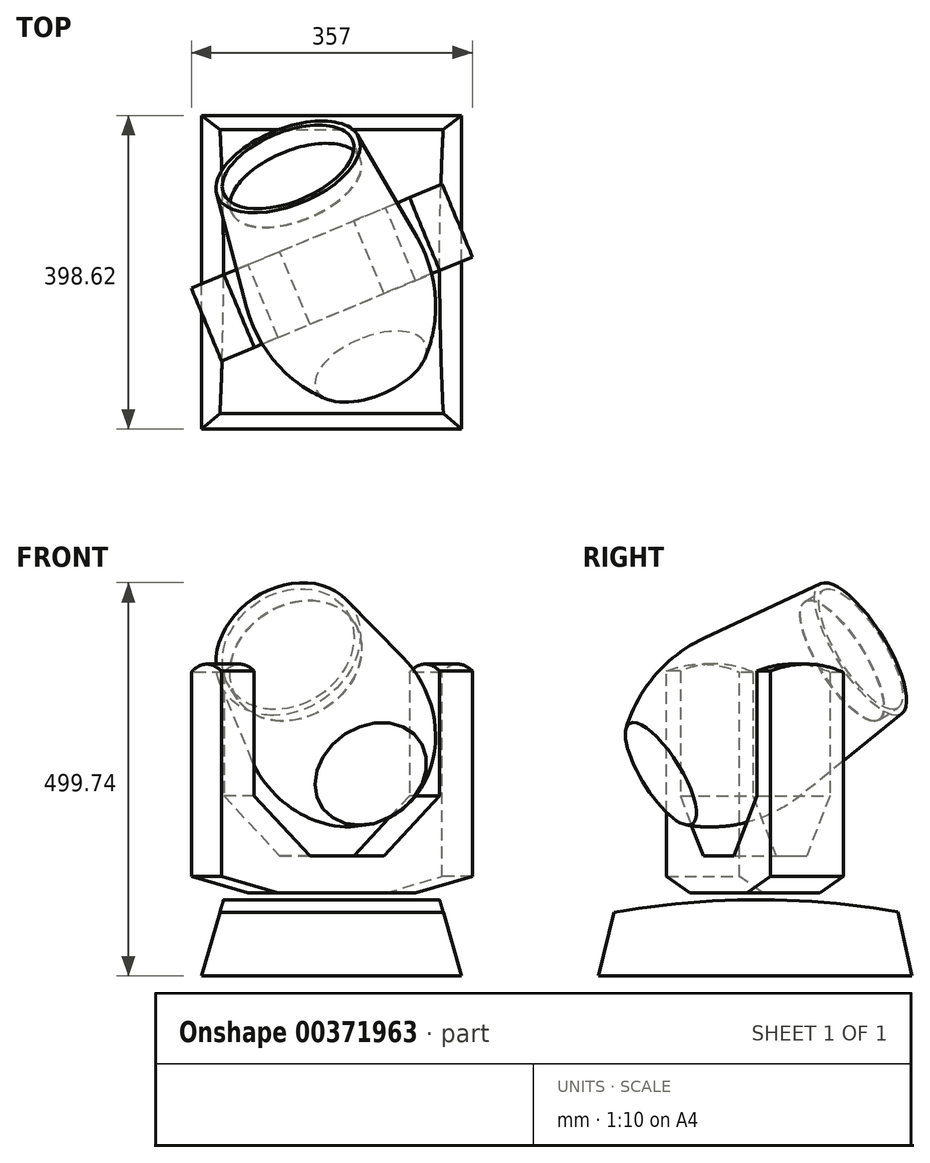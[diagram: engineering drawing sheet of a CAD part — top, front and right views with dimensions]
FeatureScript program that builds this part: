
annotation { "Feature Type Name" : "Feature", "Feature Type Description" : "" }
export const myFeature = defineFeature(function(context is Context, id is Id, definition is map)
    precondition{}
    {
        {
            var Q0;
            Q0=qCreatedBy(makeId("Front.planeOp"),FACE);
            var sketch = newSketch(context, id + "F0", { "sketchPlane" : qUnion([Q0])});
            skLineSegment(sketch, "E0.bottom", {"start": v(164.65, -50) * mm, "end": v(-165.35, -50) * mm});
            skLineSegment(sketch, "E0.top", {"start": v(136.02, 50) * mm, "end": v(-136.72, 50) * mm});
            skPoint(sketch, "E0.middle", {"position": v(0, 0) * mm});
            skLineSegment(sketch, "E1", {"start": v(-165.35, -50) * mm, "end": v(-136.72, 50) * mm});
            skLineSegment(sketch, "E2", {"start": v(164.65, -50) * mm, "end": v(136.02, 50) * mm});
            skPoint(sketch, "E0.right.end.orphan", {"position": v(-164.65, 50) * mm});
            skPoint(sketch, "E3.orphan", {"position": v(165.35, 50) * mm});
            skLineSegment(sketch, "E4", {"start": v(-0.35, -50) * mm, "end": v(-0.35, 50) * mm, "construction": true});
            skSolve(sketch);
        }
        {
            var Q0;
            Q0 = qSketchRegion(id + "F0", true);
            extrude(context, id + "F1", {"entities" : qUnion([Q0]), "depth" : 200 * mm, "hasSecondDirection" : true, "secondDirectionOppositeDirection" : true, "secondDirectionDepth" : 200 * mm});
        }
        {
            var Q0;
            Q0=qCreatedBy(makeId("Right.planeOp"),FACE);
            var sketch = newSketch(context, id + "F2", { "sketchPlane" : qUnion([Q0])});
            skLineSegment(sketch, "E5", {"start": v(199.65, -50.3) * mm, "end": v(181.5, 31.39) * mm});
            skLineSegment(sketch, "E6", {"start": v(199.65, -50.3) * mm, "end": v(-199.12, -50.3) * mm});
            skLineSegment(sketch, "E7", {"start": v(-199.12, -50.3) * mm, "end": v(-179.02, 30.74) * mm});
            skArc(sketch, "E8", {"start": v(181.5, 31.39) * mm, "mid": v(1.21, 47.02) * mm, "end": v(-179.02, 30.74) * mm});
            skLineSegment(sketch, "E9.bottom", {"start": v(207.43, 59.92) * mm, "end": v(-206.9, 59.92) * mm});
            skLineSegment(sketch, "E9.top", {"start": v(207.43, -57.44) * mm, "end": v(-206.9, -57.44) * mm});
            skLineSegment(sketch, "E9.left", {"start": v(207.43, 59.92) * mm, "end": v(207.43, -57.44) * mm});
            skLineSegment(sketch, "E9.right", {"start": v(-206.9, 59.92) * mm, "end": v(-206.9, -57.44) * mm});
            skSolve(sketch);
        }
        {
            var Q0;
            Q0 = qSketchRegion(id + "F2", true);
            extrude(context, id + "F3", {"entities" : qUnion([Q0]), "operationType" : NewBodyOperationType.REMOVE, "endBound" : BoundingType.THROUGH_ALL, "oppositeDirection" : true, "depth" : 25 * mm, "hasSecondDirection" : true, "secondDirectionBound" : SecondDirectionBoundingType.THROUGH_ALL, "secondDirectionOppositeDirection" : false, "secondDirectionDepth" : 25 * mm});
        }
        {
            var Q0;
            Q0=qCreatedBy(makeId("Front.planeOp"),FACE);
            var sketch = newSketch(context, id + "F4", { "sketchPlane" : qUnion([Q0])});
            skLineSegment(sketch, "E10", {"start": v(0, 0) * mm, "end": v(0, 55.5) * mm, "construction": true});
            skLineSegment(sketch, "E11", {"start": v(94.5, 55.5) * mm, "end": v(0, 55.5) * mm});
            skLineSegment(sketch, "E12", {"start": v(94.5, 55.5) * mm, "end": v(172.5, 76.57) * mm});
            skLineSegment(sketch, "E13", {"start": v(172.5, 76.57) * mm, "end": v(172.5, 350) * mm});
            skLineSegment(sketch, "E14", {"start": v(172.5, 350) * mm, "end": v(127.55, 350) * mm});
            skLineSegment(sketch, "E15", {"start": v(127.55, 350) * mm, "end": v(127.55, 179.09) * mm});
            skLineSegment(sketch, "E16", {"start": v(127.55, 179.09) * mm, "end": v(50.95, 102.49) * mm});
            skLineSegment(sketch, "E17", {"start": v(50.95, 102.49) * mm, "end": v(0, 102.49) * mm});
            skLineSegment(sketch, "E18.MirrorCS", {"start": v(-127.55, 179.09) * mm, "end": v(-50.95, 102.49) * mm});
            skLineSegment(sketch, "E19.MirrorCS", {"start": v(-50.95, 102.49) * mm, "end": v(0, 102.49) * mm});
            skLineSegment(sketch, "E20.MirrorCS", {"start": v(-127.55, 350) * mm, "end": v(-127.55, 179.09) * mm});
            skLineSegment(sketch, "E21.MirrorCS", {"start": v(-172.5, 350) * mm, "end": v(-127.55, 350) * mm});
            skLineSegment(sketch, "E22.MirrorCS", {"start": v(-94.5, 55.5) * mm, "end": v(0, 55.5) * mm});
            skLineSegment(sketch, "E23.MirrorCS", {"start": v(-172.5, 76.57) * mm, "end": v(-172.5, 350) * mm});
            skLineSegment(sketch, "E24.MirrorCS", {"start": v(-94.5, 55.5) * mm, "end": v(-172.5, 76.57) * mm});
            skSolve(sketch);
        }
        {
            var Q0;
            Q0 = qSketchRegion(id + "F4", true);
            extrude(context, id + "F5", {"entities" : qUnion([Q0]), "depth" : 50 * mm, "hasSecondDirection" : true, "secondDirectionOppositeDirection" : true, "secondDirectionDepth" : 50 * mm});
        }
        {
            var Q0;
            Q0=qCreatedBy(makeId("Right.planeOp"),FACE);
            var sketch = newSketch(context, id + "F6", { "sketchPlane" : qUnion([Q0])});
            skArc(sketch, "E25", {"start": v(57.41, 332.46) * mm, "mid": v(-0.95, 346.34) * mm, "end": v(-59.48, 333.23) * mm});
            skLineSegment(sketch, "E26", {"start": v(57.41, 332.46) * mm, "end": v(57.41, 368.6) * mm});
            skLineSegment(sketch, "E27", {"start": v(57.41, 368.6) * mm, "end": v(-58.72, 368.6) * mm});
            skLineSegment(sketch, "E28", {"start": v(-58.72, 368.6) * mm, "end": v(-59.48, 333.23) * mm});
            skSolve(sketch);
        }
        {
            var Q0;
            Q0 = qSketchRegion(id + "F6", true);
            extrude(context, id + "F7", {"entities" : qUnion([Q0]), "operationType" : NewBodyOperationType.REMOVE, "endBound" : BoundingType.THROUGH_ALL, "oppositeDirection" : true, "depth" : 25 * mm, "hasSecondDirection" : true, "secondDirectionBound" : SecondDirectionBoundingType.THROUGH_ALL, "secondDirectionOppositeDirection" : false, "secondDirectionDepth" : 25 * mm});
        }
        {
            var Q0;
            Q0=qCreatedBy(makeId("Right.planeOp"),FACE);
            var sketch = newSketch(context, id + "F8", { "sketchPlane" : qUnion([Q0])});
            skLineSegment(sketch, "E29", {"start": v(172.17, 264.85) * mm, "end": v(-144.94, 264.85) * mm});
            skLineSegment(sketch, "E30", {"start": v(172.17, 264.85) * mm, "end": v(172.17, 362.16) * mm});
            skLineSegment(sketch, "E31", {"start": v(172.17, 362.16) * mm, "end": v(0, 382.08) * mm});
            skArc(sketch, "E32", {"start": v(0, 382.08) * mm, "mid": v(-76.7, 375.65) * mm, "end": v(-144.94, 340.02) * mm});
            skLineSegment(sketch, "E33", {"start": v(-144.94, 264.85) * mm, "end": v(-144.94, 340.02) * mm});
            skSolve(sketch);
        }
        {
            var Q0;
            Q0 = qSketchRegion(id + "F8", true);
            var Q1;
            Q1=sQuery(id+"F8.wireOp",EDGE,"E29");
            revolve(context, id + "F9", {"entities" : qUnion([Q0]), "axis" : qUnion([Q1]), "revolveType" : RevolveType.FULL});
        }
        {
            var Q0;
            Q0=makeQuery(id+"F9.opRevolve","SWEPT_FACE",FACE,{"disambiguationData":[OSD([sQuery(id+"F8.wireOp",EDGE,"E30")])]});
            var sketch = newSketch(context, id + "F10", { "sketchPlane" : qUnion([Q0])});
            skCircle(sketch, "E34", {"center": v(0, 264.85) * mm, "radius": 88.64 * mm});
            skSolve(sketch);
        }
        {
            var Q0;
            Q0 = qSketchRegion(id + "F10", true);
            extrude(context, id + "F11", {"entities" : qUnion([Q0]), "operationType" : NewBodyOperationType.REMOVE, "oppositeDirection" : true, "depth" : 30 * mm});
        }
        {
            var Q0;
            Q0=makeQuery(id+"F11.boolean.opBoolean","COPY",FACE,{"derivedFrom":makeQuery(id+"F11.opExtrude","CAP_FACE",FACE,{"disambiguationData":[OSD([sQuery(id+"F10.wireOp",EDGE,"E34")])],"isStart":false})});
            var sketch = newSketch(context, id + "F12", { "sketchPlane" : qUnion([Q0])});
            skCircle(sketch, "E35.0", {"center": v(0, 264.85) * mm, "radius": 88.64 * mm});
            skSolve(sketch);
        }
        {
            var Q0;
            Q0 = qSketchRegion(id + "F12", true);
            extrude(context, id + "F13", {"entities" : qUnion([Q0]), "depth" : 1 * mm});
        }
        {
            var Q0;
            Q0=qCreatedBy(makeId("Top.planeOp"),FACE);
            cPlane(context, id + "F14", {"entities" : qUnion([Q0]), "cplaneType" : CPlaneType.OFFSET, "offset" : 265 * mm, "width" : 150 * mm, "height" : 150 * mm});
        }
        {
            var Q0;
            Q0=makeQuery(id+"F3.boolean.opBoolean","COPY",EDGE,{"derivedFrom":makeQuery(id+"F3.opExtrude","SWEPT_EDGE",EDGE,{"disambiguationData":[OSD([sQuery(id+"F2.wireOp",EDGE,"E5"),sQuery(id+"F2.wireOp",EDGE,"E8")])]})});
            var Q1;
            Q1=qCreatedBy(id+"F14.planeOp",FACE);
            cPlane(context, id + "F15", {"entities" : qUnion([Q0, Q1]), "cplaneType" : CPlaneType.LINE_ANGLE, "offset" : 25 * mm, "angle" : 15 * degree, "width" : 150 * mm, "height" : 150 * mm});
        }
        {
            var Q0;
            Q0=qCreatedBy(id+"F15.planeOp",FACE);
            cPlane(context, id + "F16", {"entities" : qUnion([Q0]), "cplaneType" : CPlaneType.OFFSET, "offset" : 280 * mm, "oppositeDirection" : true, "width" : 150 * mm, "height" : 150 * mm});
        }
        {
            var Q0;
            Q0=makeQuery(id+"F9.opRevolve","SWEPT_BODY",BODY,{"disambiguationData":[OSD([sQuery(id+"F8.wireOp",EDGE,"E29"),sQuery(id+"F8.wireOp",EDGE,"E30"),sQuery(id+"F8.wireOp",EDGE,"E31"),sQuery(id+"F8.wireOp",EDGE,"E32"),sQuery(id+"F8.wireOp",EDGE,"E33")])]});
            var Q1;
            Q1=makeQuery(id+"F13.opExtrude","SWEPT_BODY",BODY,{"disambiguationData":[OSD([sQuery(id+"F12.wireOp",EDGE,"E35.0")])]});
            var Q2;
            Q2=qCreatedBy(id+"F16.planeOp",FACE);
            mirror(context, id + "F17", {"entities" : qUnion([Q0, Q1]), "mirrorPlane" : qUnion([Q2])});
        }
        {
            var Q0;
            Q0=makeQuery(id+"F9.opRevolve","SWEPT_BODY",BODY,{"disambiguationData":[OSD([sQuery(id+"F8.wireOp",EDGE,"E29"),sQuery(id+"F8.wireOp",EDGE,"E30"),sQuery(id+"F8.wireOp",EDGE,"E31"),sQuery(id+"F8.wireOp",EDGE,"E32"),sQuery(id+"F8.wireOp",EDGE,"E33")])]});
            deleteBodies(context, id + "F18", {"entities" : qUnion([Q0])});
        }
        {
            var Q0;
            Q0=makeQuery(id+"F13.opExtrude","SWEPT_BODY",BODY,{"disambiguationData":[OSD([sQuery(id+"F12.wireOp",EDGE,"E35.0")])]});
            deleteBodies(context, id + "F19", {"entities" : qUnion([Q0])});
        }
        {
            var Q0;
            Q0=qCreatedBy(makeId("Front.planeOp"),FACE);
            var Q1;
            Q1=qCreatedBy(makeId("Right.planeOp"),FACE);
            cPlane(context, id + "F20", {"entities" : qUnion([Q0, Q1]), "cplaneType" : CPlaneType.MID_PLANE, "offset" : 25 * mm, "width" : 150 * mm, "height" : 150 * mm});
        }
        {
            var Q0;
            Q0=qCreatedBy(id+"F20.planeOp",FACE);
            var Q1;
            Q1=qCreatedBy(makeId("Right.planeOp"),FACE);
            cPlane(context, id + "F21", {"entities" : qUnion([Q0, Q1]), "cplaneType" : CPlaneType.MID_PLANE, "offset" : 25 * mm, "width" : 150 * mm, "height" : 150 * mm});
        }
        {
            var Q0;
            Q0=qCreatedBy(makeId("Right.planeOp"),FACE);
            var Q1;
            Q1=qCreatedBy(id+"F21.planeOp",FACE);
            cPlane(context, id + "F22", {"entities" : qUnion([Q0, Q1]), "cplaneType" : CPlaneType.MID_PLANE, "offset" : 25 * mm, "width" : 150 * mm, "height" : 150 * mm});
        }
        {
            var Q0;
            Q0=makeQuery(id+"F5.opExtrude","SWEPT_BODY",BODY,{"disambiguationData":[OSD([sQuery(id+"F4.wireOp",EDGE,"E11"),sQuery(id+"F4.wireOp",EDGE,"E12"),sQuery(id+"F4.wireOp",EDGE,"E13"),sQuery(id+"F4.wireOp",EDGE,"E14"),sQuery(id+"F4.wireOp",EDGE,"E15"),sQuery(id+"F4.wireOp",EDGE,"E16"),sQuery(id+"F4.wireOp",EDGE,"E17"),sQuery(id+"F4.wireOp",EDGE,"E18.MirrorCS"),sQuery(id+"F4.wireOp",EDGE,"E19.MirrorCS"),sQuery(id+"F4.wireOp",EDGE,"E20.MirrorCS"),sQuery(id+"F4.wireOp",EDGE,"E21.MirrorCS"),sQuery(id+"F4.wireOp",EDGE,"E22.MirrorCS"),sQuery(id+"F4.wireOp",EDGE,"E23.MirrorCS"),sQuery(id+"F4.wireOp",EDGE,"E24.MirrorCS")])]});
            var Q1;
            Q1=makeQuery(id+"F17.opPattern","COPY",BODY,{"derivedFrom":makeQuery(id+"F9.opRevolve","SWEPT_BODY",BODY,{"disambiguationData":[OSD([sQuery(id+"F8.wireOp",EDGE,"E29"),sQuery(id+"F8.wireOp",EDGE,"E30"),sQuery(id+"F8.wireOp",EDGE,"E31"),sQuery(id+"F8.wireOp",EDGE,"E32"),sQuery(id+"F8.wireOp",EDGE,"E33")])]}),"instanceName":"1"});
            var Q2;
            Q2=makeQuery(id+"F17.opPattern","COPY",BODY,{"derivedFrom":makeQuery(id+"F13.opExtrude","SWEPT_BODY",BODY,{"disambiguationData":[OSD([sQuery(id+"F12.wireOp",EDGE,"E35.0")])]}),"instanceName":"1"});
            var Q3;
            Q3=qCreatedBy(id+"F22.planeOp",FACE);
            mirror(context, id + "F23", {"entities" : qUnion([Q0, Q1, Q2]), "mirrorPlane" : qUnion([Q3])});
        }
        {
            var Q0;
            Q0=makeQuery(id+"F5.opExtrude","SWEPT_BODY",BODY,{"disambiguationData":[OSD([sQuery(id+"F4.wireOp",EDGE,"E11"),sQuery(id+"F4.wireOp",EDGE,"E12"),sQuery(id+"F4.wireOp",EDGE,"E13"),sQuery(id+"F4.wireOp",EDGE,"E14"),sQuery(id+"F4.wireOp",EDGE,"E15"),sQuery(id+"F4.wireOp",EDGE,"E16"),sQuery(id+"F4.wireOp",EDGE,"E17"),sQuery(id+"F4.wireOp",EDGE,"E18.MirrorCS"),sQuery(id+"F4.wireOp",EDGE,"E19.MirrorCS"),sQuery(id+"F4.wireOp",EDGE,"E20.MirrorCS"),sQuery(id+"F4.wireOp",EDGE,"E21.MirrorCS"),sQuery(id+"F4.wireOp",EDGE,"E22.MirrorCS"),sQuery(id+"F4.wireOp",EDGE,"E23.MirrorCS"),sQuery(id+"F4.wireOp",EDGE,"E24.MirrorCS")])]});
            var Q1;
            Q1=makeQuery(id+"F17.opPattern","COPY",BODY,{"derivedFrom":makeQuery(id+"F9.opRevolve","SWEPT_BODY",BODY,{"disambiguationData":[OSD([sQuery(id+"F8.wireOp",EDGE,"E29"),sQuery(id+"F8.wireOp",EDGE,"E30"),sQuery(id+"F8.wireOp",EDGE,"E31"),sQuery(id+"F8.wireOp",EDGE,"E32"),sQuery(id+"F8.wireOp",EDGE,"E33")])]}),"instanceName":"1"});
            var Q2;
            Q2=makeQuery(id+"F17.opPattern","COPY",BODY,{"derivedFrom":makeQuery(id+"F13.opExtrude","SWEPT_BODY",BODY,{"disambiguationData":[OSD([sQuery(id+"F12.wireOp",EDGE,"E35.0")])]}),"instanceName":"1"});
            deleteBodies(context, id + "F24", {"entities" : qUnion([Q0, Q1, Q2])});
        }
    });
